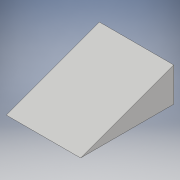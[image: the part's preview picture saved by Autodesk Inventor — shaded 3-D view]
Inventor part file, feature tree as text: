
AUTODESK INVENTOR PART (.ipt)
format: ipt  version: 2017 (Build 210142000, 142)  size: 90,624 bytes
history: native  units: in
note: dims shown in document units (in); Inventor stores cm internally (conversion verified against a paired STEP export)
features: move_body x2, extrude x1, sketch x1
ambient origin geometry x8: Origin, YZ Plane, XZ Plane, XY Plane, X Axis, Y Axis, Z Axis, Center Point
bodies: Solid1 (feature_tree)
feature tree (4):
  extrude  "Extrusion1"  Depth=1.5in
  move_body  "Move Body1"
  move_body  "Move Body2"
  sketch  "Sketch1"  dims[d2=2.0in d4=0.481in d5=1.5in d6=0.0in d7=180.0deg d8=270.0deg]
